# Revit family: LAMP_BAZZ REC SYMMETRIC
name_source: partatom
category: Modelos genéricos
revit_build: Autodesk Revit 2018 (Build: 20190510_1515(x64)
units: mm (PartAtom-declared; Revit-internal decimal feet)

## family parameters
Anfitrión = Cara
Compartido = No
Corte con vacíos al cargar = No
Cota de conector redondo = Diámetro de uso
Puede alojar armadura = No
Punto de cálculo de habitación = No
Tipo de pieza = Normal

## types (8) — shared parameters
CRI = 80
Elevación por defecto = 1219 mm
Fabricante = LAMP
Finish = Anodized matte black
Gear = Electronic
Height = 84 mm  [stored 0.275591 ft]
Installation instructions = http://www.lamp.es
Insulation class = I
LED Lifetime = 50.000 L80 B10
Lamp = MID-POWER LED
Last update = 17/02/2022
Longitud luminaria = 1043 mm  [stored 3.42192 ft]
Luminaire type = Outdoor -Recessed luminaire
MacAdam = <3
Manufacturer URL = http://www.lamp.es
Manufacturer country = Spain
Manufacturer name = LAMP
Power Supply = 220-240V 50/60Hz
Product URL = http://www.lamp.es
Product datasheet = http://www.lamp.es
Protection rating = IP67 / IK07
Type = MID POWER SAMSUNG

## per-type parameters (varying)
| type | Descripción | Dimensions | Efficacy | Initial color | Initial intensity | Modelo | Photometric web file | Plum | Power | Product code | Weight |
| 2047LM 3000 1M | BAZZ REC SYM 1M 2100 WW | 1043x106x84 | 99 lm/W | 3000 K | 2047 lm | BZ1RE100LOSY830NB | Bazz rec symmetric - base : 2047LM 3000 1M | 21 W | 19 W | BZ1RE100LOSY830NB | 5.28 kg |
| 2149LM 4000 1M | BAZZ REC SYM 1M 2100 NW | 1043x106x84 | 104 lm/W | 4000 K | 2149 lm | BZ1RE100LOSY840NB | Bazz rec symmetric - base : 2149LM 4000 1M | 21 W | 19 W | BZ1RE100LOSY840NB | 5.28 kg |
| 4024LM 3000 1M | BAZZ REC SYM 1M 4200 WW | 1043x106x84 | 101 lm/W | 3000 K | 4024 lm | BZ1RE100MOSY830NB | Bazz rec symmetric - base : 4024LM 3000 1M | 40 W | 37 W | BZ1RE100MOSY830NB | 5.38 kg |
| 4225LM 4000 1M | BAZZ REC SYM 2M 4200 WW | 1043x106x84 | 102 lm/W | 3000 K | 4094 lm | BZ1RE200LOSY830NB | Bazz rec symmetric - base : 4225LM 4000 1M | 40 W | 38 W | BZ1RE200LOSY830NB | 9.89 kg |
| 4094LM 3000 2M | BAZZ REC SYM 1M 4200 NW | 1043x106x84 | 106 lm/W | 4000 K | 4225 lm | BZ1RE100MOSY840NB | Bazz rec symmetric - base : 4094LM 3000 2M | 40 W | 37 W | BZ1RE100MOSY840NB | 5.38 kg |
| 4299LM 4000 2M | BAZZ REC SYM 2M 4200 NW | 2036x106x84 | 108 lm/W | 4000 K | 4299 lm | BZ1RE200LOSY840NB | Bazz rec symmetric - base : 4299LM 4000 2M | 40 W | 38 W | BZ1RE200LOSY840NB | 9.89 kg |
| 8048LM 3000 2M | BAZZ REC SYM 2M 8100 WW | 2036x106x84 | 105 lm/W | 3000 K | 8048 lm | BZ1RE200MOSY830NB | Bazz rec symmetric - base : 8048LM 3000 2M | 77 W | 75 W | BZ1RE200MOSY830NB | 9.89 kg |
| 8450LM 4000 2M | BAZZ REC SYM 2M 8100 NW | 2036x106x84 | 110 lm/W | 4000 K | 8450 lm | BZ1RE200MOSY840NB | Bazz rec symmetric - base : 8450LM 4000 2M | 77 W | 75 W | BZ1RE200MOSY840NB | 9.89 kg |

note: [stored X ft] marks values corroborated as IEEE doubles in the binary element streams (Revit-internal decimal feet)

## geometry (parser evidence)
native form markers: Blend x2
no freeform markers — native parametric forms only
